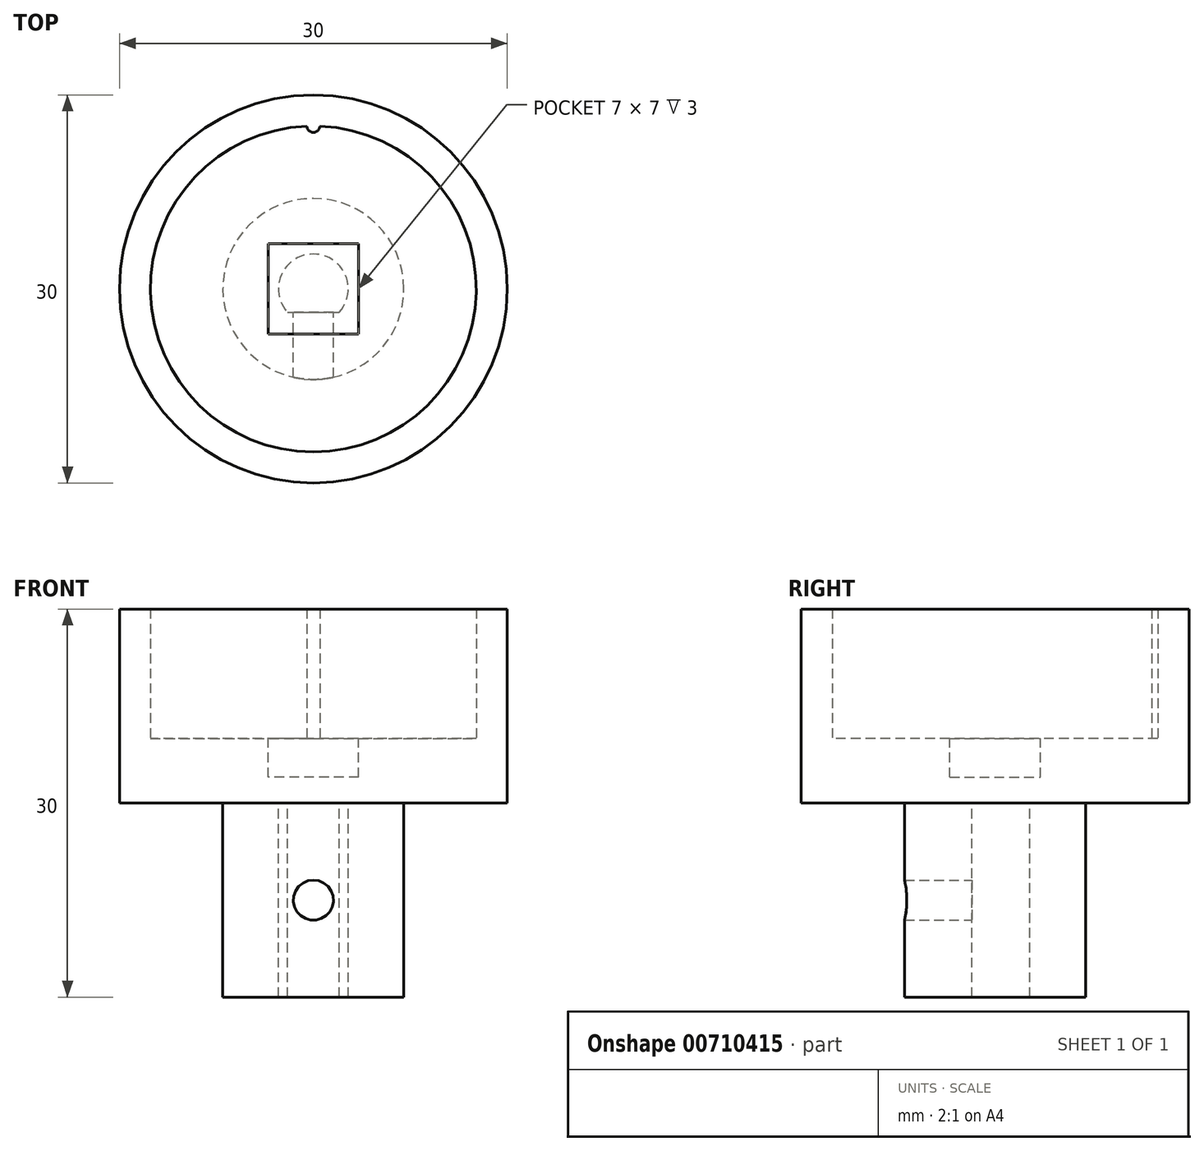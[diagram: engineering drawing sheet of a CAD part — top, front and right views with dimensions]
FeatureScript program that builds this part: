
annotation { "Feature Type Name" : "Feature", "Feature Type Description" : "" }
export const myFeature = defineFeature(function(context is Context, id is Id, definition is map)
    precondition{}
    {
        {
            var Q0;
            Q0=qCreatedBy(makeId("Top.planeOp"),FACE);
            var sketch = newSketch(context, id + "F0", { "sketchPlane" : qUnion([Q0])});
            skLineSegment(sketch, "E0", {"start": v(-2.01, -1.8) * mm, "end": v(2.01, -1.8) * mm});
            skArc(sketch, "E1", {"start": v(-2.01, -1.8) * mm, "mid": v(0, 2.7) * mm, "end": v(2.01, -1.8) * mm});
            skCircle(sketch, "E2", {"center": v(0, 0) * mm, "radius": 15 * mm});
            skCircle(sketch, "E3", {"center": v(0, 0) * mm, "radius": 7 * mm});
            skCircle(sketch, "E4", {"center": v(0, 0) * mm, "radius": 12.6 * mm});
            skArc(sketch, "E5", {"start": v(-0.5, 12.6) * mm, "mid": v(0, 12.1) * mm, "end": v(0.5, 12.6) * mm});
            skSolve(sketch);
        }
        {
            var Q0;
            Q0=makeQuery(id+"F0.imprint","IMPRINT",FACE,{"disambiguationData":[TD([[makeQuery(id+"F0.imprint","IMPRINT",EDGE,{"derivedFrom":sQuery(id+"F0.wireOp",EDGE,"E0")}),-1.0]])]});
            var Q1;
            Q1=sQuery(id+"F0.wireOp",EDGE,"E1");
            var Q2;
            Q2=sQuery(id+"F0.wireOp",EDGE,"E0");
            extrude(context, id + "F1", {"entities" : qUnion([Q0]), "surfaceEntities" : qUnion([Q1, Q2]), "oppositeDirection" : true, "depth" : 15 * mm, "offsetDistance" : 25 * mm});
        }
        {
            var Q0;
            Q0=makeQuery(id+"F0.imprint","IMPRINT",FACE,{"disambiguationData":[TD([[makeQuery(id+"F0.imprint","IMPRINT",EDGE,{"derivedFrom":sQuery(id+"F0.wireOp",EDGE,"E3")}),-1.0]])]});
            var Q1;
            Q1=makeQuery(id+"F0.imprint","IMPRINT",FACE,{"disambiguationData":[TD([[makeQuery(id+"F0.imprint","IMPRINT",EDGE,{"derivedFrom":sQuery(id+"F0.wireOp",EDGE,"E0")}),1.0]])]});
            var Q2;
            Q2=makeQuery(id+"F0.imprint","IMPRINT",FACE,{"disambiguationData":[TD([[makeQuery(id+"F0.imprint","IMPRINT",EDGE,{"derivedFrom":sQuery(id+"F0.wireOp",EDGE,"E0")}),-1.0]])]});
            extrude(context, id + "F2", {"entities" : qUnion([Q0, Q1, Q2]), "operationType" : NewBodyOperationType.ADD, "depth" : 5 * mm, "offsetDistance" : 25 * mm});
        }
        {
            var Q0;
            Q0=makeQuery(id+"F0.imprint","IMPRINT",FACE,{"disambiguationData":[TD([[makeQuery(id+"F0.imprint","IMPRINT",EDGE,{"derivedFrom":sQuery(id+"F0.wireOp",EDGE,"E2")}),1.0]])]});
            extrude(context, id + "F3", {"entities" : qUnion([Q0]), "operationType" : NewBodyOperationType.ADD, "depth" : 15 * mm, "offsetDistance" : 25 * mm});
        }
        {
            var Q0;
            {var subQ0=sQuery(id+"F0.wireOp",EDGE,"E0");Q0=makeQuery(id+"F2.boolean.opBoolean","MERGE",FACE,{"derivedFrom":[makeQuery(id+"F1.opExtrude","SWEPT_FACE",FACE,{"disambiguationData":[OSD([subQ0])]}),makeQuery(id+"F2.opExtrude","SWEPT_FACE",FACE,{"disambiguationData":[OSD([subQ0])]})]});}
            var sketch = newSketch(context, id + "F4", { "sketchPlane" : qUnion([Q0])});
            skPoint(sketch, "E6", {"position": v(0, -7.5) * mm});
            skSolve(sketch);
        }
        {
            var Q0;
            Q0=sQuery(id+"F4.wireOp",VERTEX,"E6");
            var Q1;
            Q1=makeQuery(id+"F1.opExtrude","SWEPT_BODY",BODY,{"disambiguationData":[OSD([sQuery(id+"F0.wireOp",EDGE,"E0"),sQuery(id+"F0.wireOp",EDGE,"E1"),sQuery(id+"F0.wireOp",EDGE,"E3")])]});
            hole(context, id + "F5", {"style" : HoleStyle.SIMPLE, "endStyle" : HoleEndStyle.THROUGH, "holeDiameter" : 3.1 * mm, "majorDiameter" : 5 * mm, "isTappedThrough" : true, "tappedDepth" : 12 * mm, "tapClearance" : 3, "locations" : qUnion([Q0]), "scope" : qUnion([Q1])});
        }
        {
            var Q0;
            {var subQ0=sQuery(id+"F0.wireOp",EDGE,"E5");Q0=makeQuery(id+"F0.imprint","IMPRINT",FACE,{"disambiguationData":[TD([[makeQuery(id+"F0.imprint","IMPRINT",EDGE,{"derivedFrom":subQ0}),1.0]])]});}
            extrude(context, id + "F6", {"entities" : qUnion([Q0]), "operationType" : NewBodyOperationType.ADD, "depth" : 15 * mm, "offsetDistance" : 25 * mm});
        }
        {
            var Q0;
            Q0=makeQuery(id+"F2.opExtrude","CAP_FACE",FACE,{"disambiguationData":[OSD([sQuery(id+"F0.wireOp",EDGE,"E4"),sQuery(id+"F0.wireOp",EDGE,"E5")])],"isStart":false});
            var sketch = newSketch(context, id + "F7", { "sketchPlane" : qUnion([Q0])});
            skLineSegment(sketch, "E7.bottom", {"start": v(3.5, -3.5) * mm, "end": v(-3.5, -3.5) * mm});
            skLineSegment(sketch, "E7.top", {"start": v(3.5, 3.5) * mm, "end": v(-3.5, 3.5) * mm});
            skLineSegment(sketch, "E7.left", {"start": v(3.5, -3.5) * mm, "end": v(3.5, 3.5) * mm});
            skLineSegment(sketch, "E7.right", {"start": v(-3.5, -3.5) * mm, "end": v(-3.5, 3.5) * mm});
            skPoint(sketch, "E7.middle", {"position": v(0, 0) * mm});
            skSolve(sketch);
        }
        {
            var Q0;
            Q0=makeQuery(id+"F7.imprint","IMPRINT",FACE,{"disambiguationData":[TD([[makeQuery(id+"F7.imprint","IMPRINT",EDGE,{"derivedFrom":sQuery(id+"F7.wireOp",EDGE,"E7.bottom")}),-1.0]])]});
            extrude(context, id + "F8", {"entities" : qUnion([Q0]), "operationType" : NewBodyOperationType.REMOVE, "oppositeDirection" : true, "depth" : 3 * mm, "offsetDistance" : 25 * mm});
        }
    });
